# Revit family: FS_Стол_Модерн садовый_R16
name_source: partatom
category: Антураж
revit_build: Autodesk Revit 2016 (Build: 20160314_0715(x64)
units: mm (PartAtom-declared; Revit-internal decimal feet)

## family parameters
Всегда вертикально = Да
Источник визуального образа = Геометрия семейства
На основе рабочей плоскости = Нет
Общий = Нет
При загрузке вырезать с полостями = Нет
Точка расчета площади = Нет

## types (2) — shared parameters
ADSK_Код изделия = 6732
ADSK_Материал доски = FS_Древесина
ADSK_Материал крепления = FS_Цинк
ADSK_Материал опоры = FS_Чугун
ADSK_Размер_Высота = 600 мм
ADSK_Размер_Ширина = 1200 мм
URL = https://hobbyka.ru
Изготовитель = ООО 'Хоббика'
Комментарии к типоразмеру = Материалы: сталь, брус
zero-valued in all types: Высота

## per-type parameters (varying)
| type | ADSK_Размер_Длина | Стоимость |
| Стол садовый «Модерн» 3.0м | 3000 мм | 34178 $ |
| Стол садовый «Модерн» 2.0м | 2000 мм | 23042 $ |

note: column(s) folded — value = type name in every type: ADSK_Наименование
